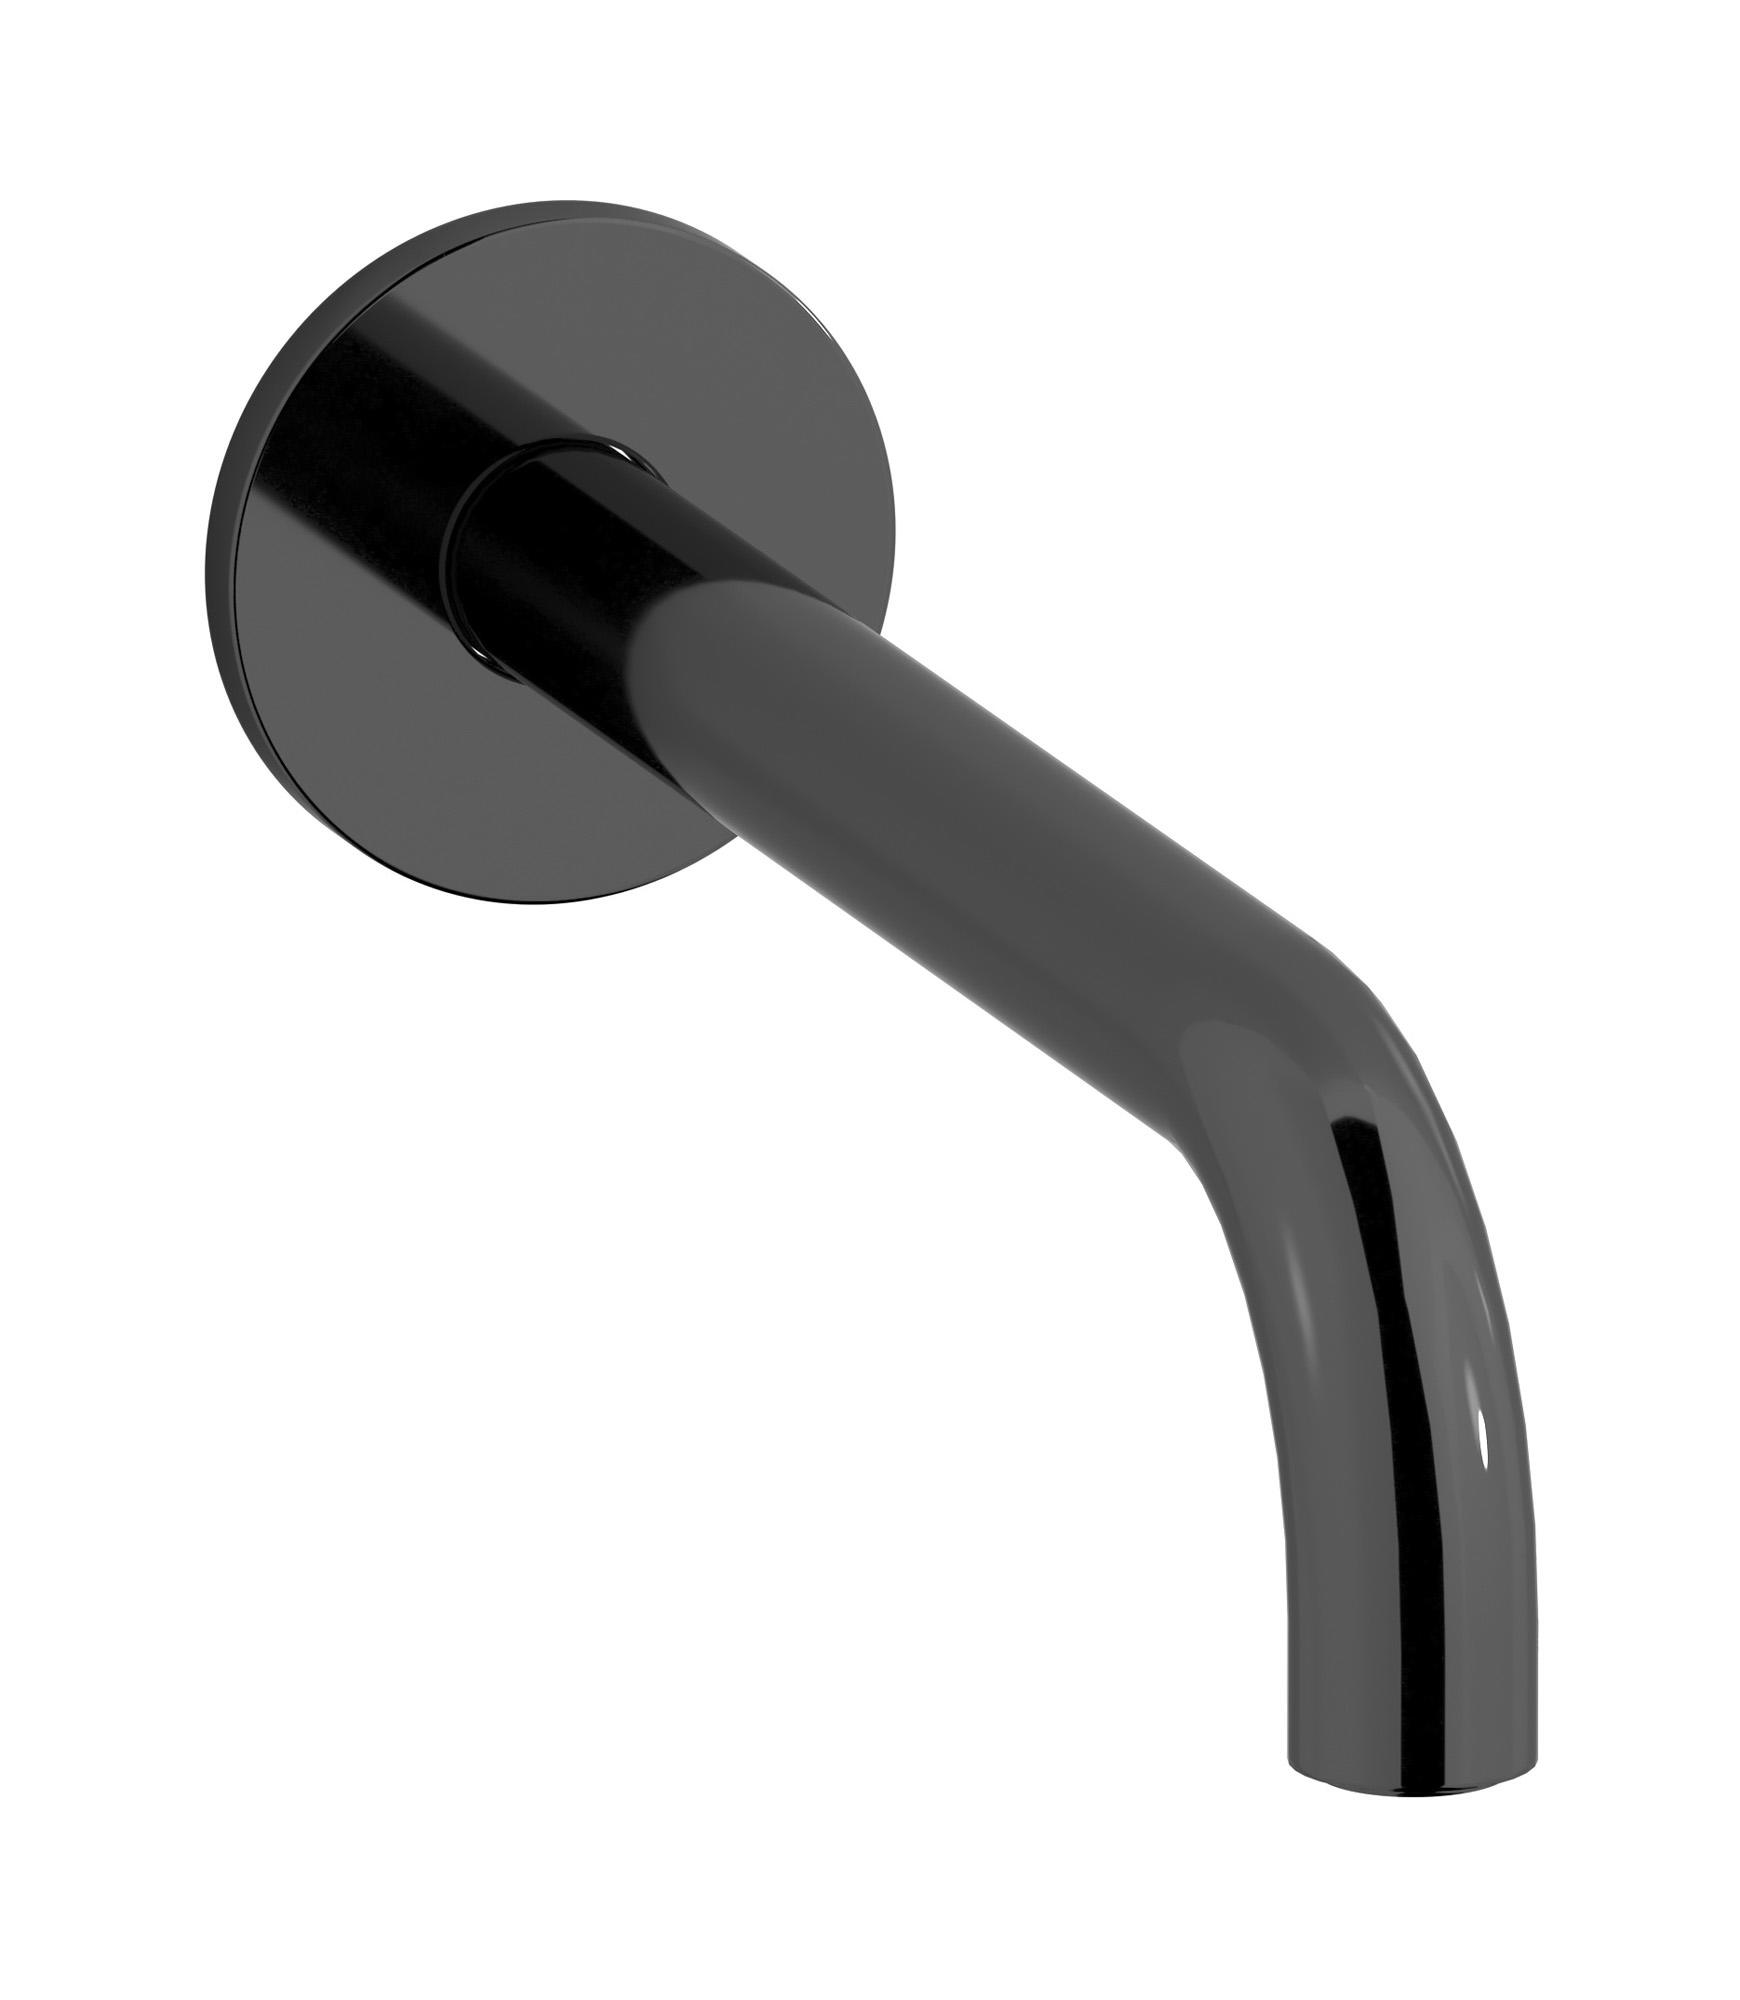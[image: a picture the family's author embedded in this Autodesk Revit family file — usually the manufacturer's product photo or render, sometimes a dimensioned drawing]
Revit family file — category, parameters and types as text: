
# Revit family: RX327
name_source: partatom
category: Apparecchi idraulici
units: mm (PartAtom-declared; Revit-internal decimal feet)

## family parameters
Basato su piano di lavoro = No
Condiviso = No
Mantieni orientamento annotazione = No
Numero OmniClass = 23.45.55.17
Punto di calcolo locali = No
Quota connettore circolare = Usa diametro
Sempre verticale = Sì
Taglio con vuoti quando caricato = No
Tipo di parte = Normale
Titolo OmniClass = Mixing Faucets

## types (12) — shared parameters
Commenti sul tipo = Wall mounted spout
Connessione CW = No
Connessione HW = No
Connessione di scarico = No
Connessione di ventilazione = No
Descrizione = Wall mounted spout
Produttore = IB Rubinetterie S.p.A.
URL = https://www.weareib.it
Water inlet = 10 mm  [stored 0.0328084 ft]
zero-valued in all types: Prospetto di default

## per-type parameters (varying)
| type | Finishes surface | Immagine tipo | Modello |
| Chrome | IB_Chrome | RX327CC.jpg | RX327CC |
| Black Chrome | IB_Black chrome | RX327CF.jpg | RX327CF |
| Brushed Black Chrome | IB_Brushed black chrome | RX327CS.jpg | RX327CS |
| Pale Gold | IB_Pale gold | RX327II.jpg | RX327II |
| Brushed Pale Gold | IB_brushed pale gold | RX327IS.jpg | RX327IS |
| Matt Black | IB_matt black | RX327NP.jpg | RX327NP |
| Natural Brass | IB_Brass | RX327ON.jpg | RX327ON |
| Gold | IB_gold | RX327OO.jpg | RX327OO |
| Brushed Gold | IB_brushed gold | RX327OS.jpg | RX327OS |
| Rose Gold | IB_Rose gold | RX327RS.jpg | RX327RS |
| Brushed Rose Gold | IB_Brushed rose gold | RX327SR.jpg | RX327SR |
| Brushed Nickel | IB_Brushed nickel | RX327SS.jpg | RX327SS |

note: [stored X ft] marks values corroborated as IEEE doubles in the binary element streams (Revit-internal decimal feet)
